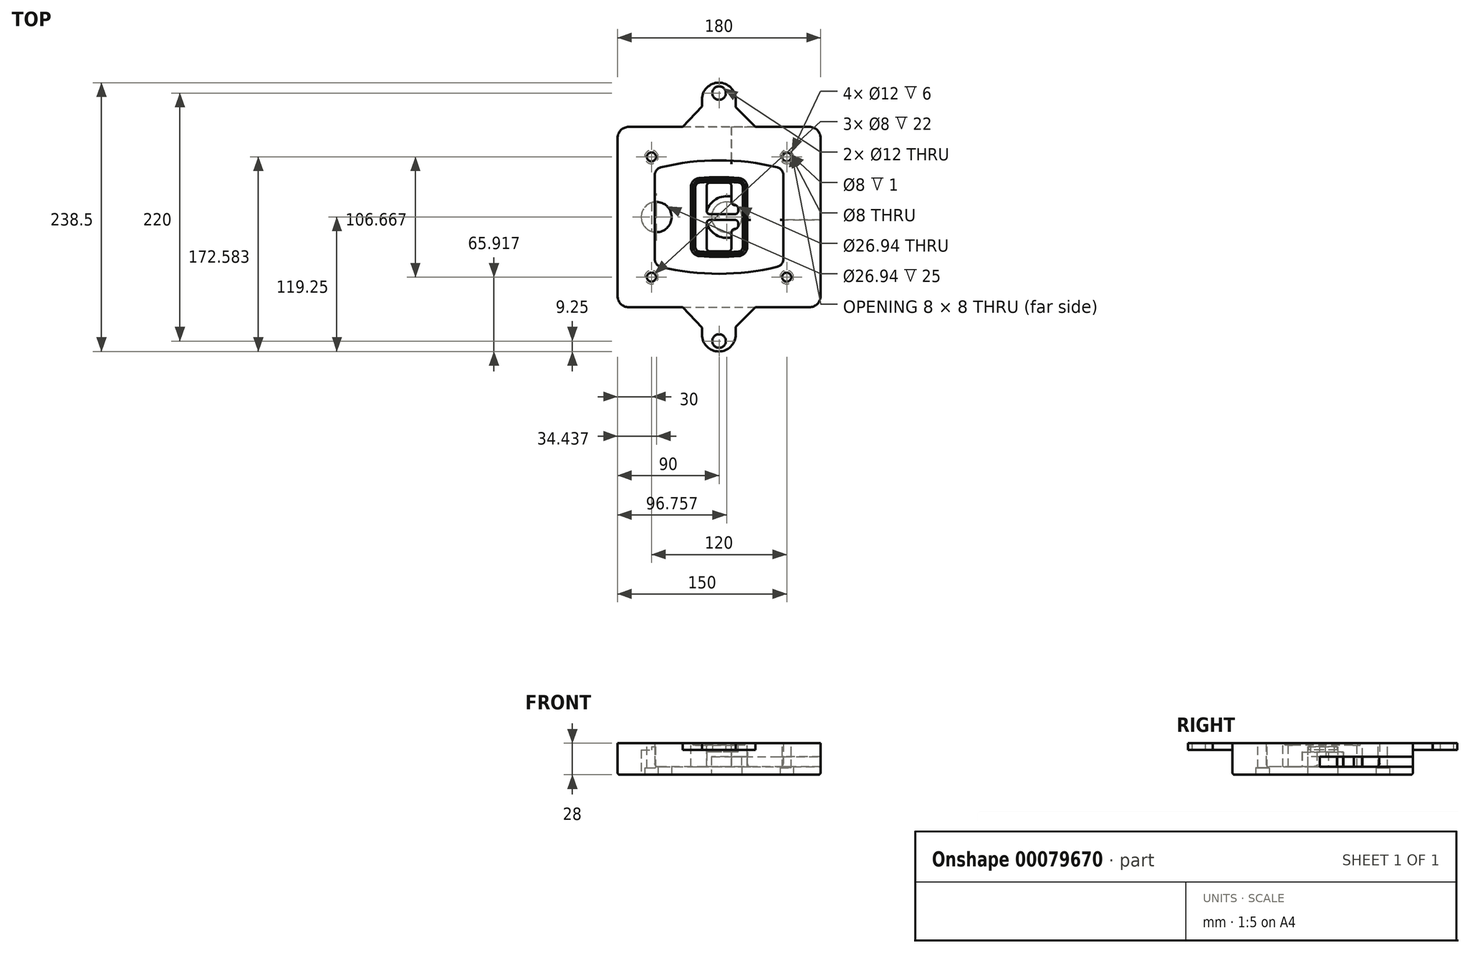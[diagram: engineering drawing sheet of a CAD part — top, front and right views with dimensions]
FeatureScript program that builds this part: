
annotation { "Feature Type Name" : "Feature", "Feature Type Description" : "" }
export const myFeature = defineFeature(function(context is Context, id is Id, definition is map)
    precondition{}
    {
        {
            var Q0;
            Q0=qCreatedBy(makeId("Top.planeOp"),FACE);
            var sketch = newSketch(context, id + "F0", { "sketchPlane" : qUnion([Q0])});
            skPoint(sketch, "E0.rect.middle", {"position": v(0, 0) * mm});
            skLineSegment(sketch, "E1.bottom", {"start": v(-80, -80) * mm, "end": v(80, -80) * mm});
            skLineSegment(sketch, "E1.top", {"start": v(-80, 80) * mm, "end": v(80, 80) * mm});
            skLineSegment(sketch, "E1.left", {"start": v(-90, -70) * mm, "end": v(-90, 70) * mm});
            skLineSegment(sketch, "E1.right", {"start": v(90, -70) * mm, "end": v(90, 70) * mm});
            skLineSegment(sketch, "E2", {"start": v(-90, 80) * mm, "end": v(90, -80) * mm, "construction": true});
            skLineSegment(sketch, "E3", {"start": v(90, 80) * mm, "end": v(-90, -80) * mm, "construction": true});
            skCircle(sketch, "E4", {"center": v(-60, 53.33) * mm, "radius": 4 * mm});
            skCircle(sketch, "E5", {"center": v(60, 53.33) * mm, "radius": 4 * mm});
            skCircle(sketch, "E6", {"center": v(60, -53.33) * mm, "radius": 4 * mm});
            skCircle(sketch, "E7", {"center": v(-60, -53.33) * mm, "radius": 4 * mm});
            skLineSegment(sketch, "E8", {"start": v(-60, 53.33) * mm, "end": v(60, 53.33) * mm, "construction": true});
            skLineSegment(sketch, "E9", {"start": v(60, 53.33) * mm, "end": v(60, -53.33) * mm, "construction": true});
            skLineSegment(sketch, "E10", {"start": v(60, -53.33) * mm, "end": v(-60, -53.33) * mm, "construction": true});
            skLineSegment(sketch, "E11", {"start": v(-60, -53.33) * mm, "end": v(-60, 53.33) * mm, "construction": true});
            skLineSegment(sketch, "E12", {"start": v(-60, 37.3) * mm, "end": v(-60, -37.3) * mm});
            skLineSegment(sketch, "E13", {"start": v(60, 37.3) * mm, "end": v(60, -37.3) * mm});
            skArc(sketch, "E14", {"start": v(52.38, 47.01) * mm, "mid": v(0, 53.33) * mm, "end": v(-52.38, 47.01) * mm});
            skArc(sketch, "E15", {"start": v(-52.38, -47.01) * mm, "mid": v(0, -53.33) * mm, "end": v(52.38, -47.01) * mm});
            skLineSegment(sketch, "E16", {"start": v(-60, 0) * mm, "end": v(60, 0) * mm, "construction": true});
            skPoint(sketch, "E17.visualSharp", {"position": v(-60, -45) * mm});
            skArc(sketch, "E17.filletArc", {"start": v(-60, -37.3) * mm, "mid": v(-57.87, -43.47) * mm, "end": v(-52.38, -47.01) * mm});
            skPoint(sketch, "E18.visualSharp", {"position": v(-60, 45) * mm});
            skArc(sketch, "E18.filletArc", {"start": v(-52.38, 47.01) * mm, "mid": v(-57.87, 43.47) * mm, "end": v(-60, 37.3) * mm});
            skPoint(sketch, "E19.visualSharp", {"position": v(60, 45) * mm});
            skArc(sketch, "E19.filletArc", {"start": v(60, 37.3) * mm, "mid": v(57.87, 43.47) * mm, "end": v(52.38, 47.01) * mm});
            skPoint(sketch, "E20.visualSharp", {"position": v(60, -45) * mm});
            skArc(sketch, "E20.filletArc", {"start": v(52.38, -47.01) * mm, "mid": v(57.87, -43.47) * mm, "end": v(60, -37.3) * mm});
            skPoint(sketch, "E21.visualSharp", {"position": v(-90, 80) * mm});
            skArc(sketch, "E21.filletArc", {"start": v(-80, 80) * mm, "mid": v(-87.07, 77.07) * mm, "end": v(-90, 70) * mm});
            skPoint(sketch, "E22.visualSharp", {"position": v(90, 80) * mm});
            skArc(sketch, "E22.filletArc", {"start": v(90, 70) * mm, "mid": v(87.07, 77.07) * mm, "end": v(80, 80) * mm});
            skPoint(sketch, "E23.visualSharp", {"position": v(90, -80) * mm});
            skArc(sketch, "E23.filletArc", {"start": v(80, -80) * mm, "mid": v(87.07, -77.07) * mm, "end": v(90, -70) * mm});
            skPoint(sketch, "E24.visualSharp", {"position": v(-90, -80) * mm});
            skArc(sketch, "E24.filletArc", {"start": v(-90, -70) * mm, "mid": v(-87.07, -77.07) * mm, "end": v(-80, -80) * mm});
            skArc(sketch, "E25.0", {"start": v(57, 37.3) * mm, "mid": v(55.5, 41.62) * mm, "end": v(51.67, 44.1) * mm});
            skLineSegment(sketch, "E25.1", {"start": v(57, 37.3) * mm, "end": v(57, -37.3) * mm});
            skArc(sketch, "E25.2", {"start": v(51.67, -44.1) * mm, "mid": v(55.5, -41.62) * mm, "end": v(57, -37.3) * mm});
            skArc(sketch, "E25.3", {"start": v(-51.67, -44.1) * mm, "mid": v(0, -50.33) * mm, "end": v(51.67, -44.1) * mm});
            skArc(sketch, "E25.4", {"start": v(-57, -37.3) * mm, "mid": v(-55.5, -41.62) * mm, "end": v(-51.67, -44.1) * mm});
            skArc(sketch, "E25.5", {"start": v(51.67, 44.1) * mm, "mid": v(0, 50.33) * mm, "end": v(-51.67, 44.1) * mm});
            skLineSegment(sketch, "E25.6", {"start": v(-57, 37.3) * mm, "end": v(-57, -37.3) * mm});
            skArc(sketch, "E25.7", {"start": v(-51.67, 44.1) * mm, "mid": v(-55.5, 41.62) * mm, "end": v(-57, 37.3) * mm});
            skArc(sketch, "E26.0", {"start": v(-53.33, 50.9) * mm, "mid": v(-61.01, 45.94) * mm, "end": v(-64, 37.3) * mm});
            skArc(sketch, "E26.1", {"start": v(53.33, 50.9) * mm, "mid": v(0, 57.33) * mm, "end": v(-53.33, 50.9) * mm});
            skArc(sketch, "E26.2", {"start": v(64, 37.3) * mm, "mid": v(61.01, 45.94) * mm, "end": v(53.33, 50.9) * mm});
            skLineSegment(sketch, "E26.3", {"start": v(64, 37.3) * mm, "end": v(64, -37.3) * mm});
            skArc(sketch, "E26.4", {"start": v(53.33, -50.9) * mm, "mid": v(61.01, -45.94) * mm, "end": v(64, -37.3) * mm});
            skLineSegment(sketch, "E26.5", {"start": v(-64, 37.3) * mm, "end": v(-64, -37.3) * mm});
            skArc(sketch, "E26.6", {"start": v(-53.33, -50.9) * mm, "mid": v(0, -57.33) * mm, "end": v(53.33, -50.9) * mm});
            skArc(sketch, "E26.7", {"start": v(-64, -37.3) * mm, "mid": v(-61.01, -45.94) * mm, "end": v(-53.33, -50.9) * mm});
            skSolve(sketch);
        }
        {
            var Q0;
            Q0=makeQuery(id+"F0.imprint","IMPRINT",FACE,{"disambiguationData":[TD([[makeQuery(id+"F0.imprint","IMPRINT",EDGE,{"derivedFrom":sQuery(id+"F0.wireOp",EDGE,"E1.bottom")}),1.0]])]});
            var Q1;
            Q1=makeQuery(id+"F0.imprint","IMPRINT",FACE,{"disambiguationData":[TD([[makeQuery(id+"F0.imprint","IMPRINT",EDGE,{"derivedFrom":sQuery(id+"F0.wireOp",EDGE,"E12")}),1.0]])]});
            var Q2;
            Q2=makeQuery(id+"F0.imprint","IMPRINT",FACE,{"disambiguationData":[TD([[makeQuery(id+"F0.imprint","IMPRINT",EDGE,{"derivedFrom":sQuery(id+"F0.wireOp",EDGE,"E25.0")}),1.0]])]});
            var Q3;
            Q3=makeQuery(id+"F0.imprint","IMPRINT",FACE,{"disambiguationData":[TD([[makeQuery(id+"F0.imprint","IMPRINT",EDGE,{"derivedFrom":sQuery(id+"F0.wireOp",EDGE,"E12")}),-1.0]])]});
            extrude(context, id + "F1", {"entities" : qUnion([Q0, Q1, Q2, Q3]), "oppositeDirection" : true, "depth" : 25 * mm});
        }
        {
            var Q0;
            Q0=makeQuery(id+"F0.imprint","IMPRINT",FACE,{"disambiguationData":[TD([[makeQuery(id+"F0.imprint","IMPRINT",EDGE,{"derivedFrom":sQuery(id+"F0.wireOp",EDGE,"E12")}),1.0]])]});
            extrude(context, id + "F2", {"entities" : qUnion([Q0]), "operationType" : NewBodyOperationType.ADD, "depth" : 3 * mm});
        }
        {
            var Q0;
            Q0=makeQuery(id+"F0.imprint","IMPRINT",FACE,{"disambiguationData":[TD([[makeQuery(id+"F0.imprint","IMPRINT",EDGE,{"derivedFrom":sQuery(id+"F0.wireOp",EDGE,"E25.0")}),1.0]])]});
            extrude(context, id + "F3", {"entities" : qUnion([Q0]), "operationType" : NewBodyOperationType.REMOVE, "oppositeDirection" : true, "depth" : 18 * mm});
        }
        {
            var Q0;
            Q0=makeQuery(id+"F2.opExtrude","CAP_FACE",FACE,{"disambiguationData":[OSD([sQuery(id+"F0.wireOp",EDGE,"E12"),sQuery(id+"F0.wireOp",EDGE,"E13"),sQuery(id+"F0.wireOp",EDGE,"E14"),sQuery(id+"F0.wireOp",EDGE,"E15"),sQuery(id+"F0.wireOp",EDGE,"E17.filletArc"),sQuery(id+"F0.wireOp",EDGE,"E18.filletArc"),sQuery(id+"F0.wireOp",EDGE,"E19.filletArc"),sQuery(id+"F0.wireOp",EDGE,"E20.filletArc"),sQuery(id+"F0.wireOp",EDGE,"E25.0"),sQuery(id+"F0.wireOp",EDGE,"E25.1"),sQuery(id+"F0.wireOp",EDGE,"E25.2"),sQuery(id+"F0.wireOp",EDGE,"E25.3"),sQuery(id+"F0.wireOp",EDGE,"E25.4"),sQuery(id+"F0.wireOp",EDGE,"E25.5"),sQuery(id+"F0.wireOp",EDGE,"E25.6"),sQuery(id+"F0.wireOp",EDGE,"E25.7")])],"isStart":false});
            var sketch = newSketch(context, id + "F4", { "sketchPlane" : qUnion([Q0])});
            skArc(sketch, "E27.0", {"start": v(-17.7, -34.56) * mm, "mid": v(0, -35.33) * mm, "end": v(17.7, -34.56) * mm});
            skArc(sketch, "E28.0", {"start": v(17.7, 34.56) * mm, "mid": v(0, 35.33) * mm, "end": v(-17.7, 34.56) * mm});
            skLineSegment(sketch, "E29", {"start": v(-25, 26.59) * mm, "end": v(-25, -26.59) * mm});
            skLineSegment(sketch, "E30", {"start": v(25, 26.59) * mm, "end": v(25, -26.59) * mm});
            skLineSegment(sketch, "E31", {"start": v(-25, 33.78) * mm, "end": v(25, 33.78) * mm, "construction": true});
            skLineSegment(sketch, "E32", {"start": v(-25, -33.78) * mm, "end": v(25, -33.78) * mm, "construction": true});
            skPoint(sketch, "E33.visualSharp", {"position": v(-25, 33.78) * mm});
            skArc(sketch, "E33.filletArc", {"start": v(-17.7, 34.56) * mm, "mid": v(-22.9, 32) * mm, "end": v(-25, 26.59) * mm});
            skPoint(sketch, "E34.visualSharp", {"position": v(25, 33.78) * mm});
            skArc(sketch, "E34.filletArc", {"start": v(25, 26.59) * mm, "mid": v(22.9, 32) * mm, "end": v(17.7, 34.56) * mm});
            skPoint(sketch, "E35.visualSharp", {"position": v(25, -33.78) * mm});
            skArc(sketch, "E35.filletArc", {"start": v(17.7, -34.56) * mm, "mid": v(22.9, -32) * mm, "end": v(25, -26.59) * mm});
            skPoint(sketch, "E36.visualSharp", {"position": v(-25, -33.78) * mm});
            skArc(sketch, "E36.filletArc", {"start": v(-25, -26.59) * mm, "mid": v(-22.9, -32) * mm, "end": v(-17.7, -34.56) * mm});
            skArc(sketch, "E37.0", {"start": v(51.67, 44.1) * mm, "mid": v(0, 50.33) * mm, "end": v(-51.67, 44.1) * mm});
            skArc(sketch, "E37.1", {"start": v(-51.67, 44.1) * mm, "mid": v(-55.5, 41.62) * mm, "end": v(-57, 37.3) * mm});
            skLineSegment(sketch, "E37.2", {"start": v(-57, 37.3) * mm, "end": v(-57, -37.3) * mm});
            skArc(sketch, "E37.3", {"start": v(-57, -37.3) * mm, "mid": v(-55.5, -41.62) * mm, "end": v(-51.67, -44.1) * mm});
            skArc(sketch, "E37.4", {"start": v(-51.67, -44.1) * mm, "mid": v(0, -50.33) * mm, "end": v(51.67, -44.1) * mm});
            skArc(sketch, "E37.5", {"start": v(51.67, -44.1) * mm, "mid": v(55.5, -41.62) * mm, "end": v(57, -37.3) * mm});
            skLineSegment(sketch, "E37.6", {"start": v(57, 37.3) * mm, "end": v(57, -37.3) * mm});
            skArc(sketch, "E37.7", {"start": v(57, 37.3) * mm, "mid": v(55.5, 41.62) * mm, "end": v(51.67, 44.1) * mm});
            skLineSegment(sketch, "E38.0", {"start": v(23, 26.59) * mm, "end": v(23, -26.59) * mm});
            skArc(sketch, "E38.1", {"start": v(17.53, -32.56) * mm, "mid": v(21.42, -30.64) * mm, "end": v(23, -26.59) * mm});
            skArc(sketch, "E38.2", {"start": v(-17.53, -32.56) * mm, "mid": v(0, -33.33) * mm, "end": v(17.53, -32.56) * mm});
            skArc(sketch, "E38.3", {"start": v(-23, -26.59) * mm, "mid": v(-21.42, -30.64) * mm, "end": v(-17.53, -32.56) * mm});
            skLineSegment(sketch, "E38.4", {"start": v(-23, 26.59) * mm, "end": v(-23, -26.59) * mm});
            skArc(sketch, "E38.5", {"start": v(23, 26.59) * mm, "mid": v(21.42, 30.64) * mm, "end": v(17.53, 32.56) * mm});
            skArc(sketch, "E38.6", {"start": v(-17.53, 32.56) * mm, "mid": v(-21.42, 30.64) * mm, "end": v(-23, 26.59) * mm});
            skArc(sketch, "E38.7", {"start": v(17.53, 32.56) * mm, "mid": v(0, 33.33) * mm, "end": v(-17.53, 32.56) * mm});
            skArc(sketch, "E39.0", {"start": v(21, 26.59) * mm, "mid": v(19.95, 29.29) * mm, "end": v(17.35, 30.57) * mm});
            skLineSegment(sketch, "E39.1", {"start": v(21, 26.59) * mm, "end": v(21, -26.59) * mm});
            skArc(sketch, "E39.2", {"start": v(17.35, -30.57) * mm, "mid": v(19.95, -29.29) * mm, "end": v(21, -26.59) * mm});
            skArc(sketch, "E39.3", {"start": v(-17.35, -30.57) * mm, "mid": v(0, -31.33) * mm, "end": v(17.35, -30.57) * mm});
            skArc(sketch, "E39.4", {"start": v(-21, -26.59) * mm, "mid": v(-19.95, -29.29) * mm, "end": v(-17.35, -30.57) * mm});
            skArc(sketch, "E39.5", {"start": v(17.35, 30.57) * mm, "mid": v(0, 31.33) * mm, "end": v(-17.35, 30.57) * mm});
            skLineSegment(sketch, "E39.6", {"start": v(-21, 26.59) * mm, "end": v(-21, -26.59) * mm});
            skArc(sketch, "E39.7", {"start": v(-17.35, 30.57) * mm, "mid": v(-19.95, 29.29) * mm, "end": v(-21, 26.59) * mm});
            skLineSegment(sketch, "E40", {"start": v(-25, 0) * mm, "end": v(25, 0) * mm, "construction": true});
            skLineSegment(sketch, "E41", {"start": v(-11, 5.5) * mm, "end": v(-11, 27.5) * mm});
            skLineSegment(sketch, "E42", {"start": v(-8, 30.5) * mm, "end": v(8, 30.5) * mm});
            skLineSegment(sketch, "E43", {"start": v(11, 27.5) * mm, "end": v(11, 13.5) * mm});
            skLineSegment(sketch, "E44", {"start": v(14, 10.5) * mm, "end": v(14, 10.5) * mm});
            skLineSegment(sketch, "E45", {"start": v(17, 7.5) * mm, "end": v(17, 5.5) * mm});
            skLineSegment(sketch, "E46", {"start": v(14, 2.5) * mm, "end": v(-8, 2.5) * mm});
            skPoint(sketch, "E47.visualSharp", {"position": v(-11, 30.5) * mm});
            skArc(sketch, "E47.filletArc", {"start": v(-8, 30.5) * mm, "mid": v(-10.12, 29.62) * mm, "end": v(-11, 27.5) * mm});
            skPoint(sketch, "E48.visualSharp", {"position": v(11, 30.5) * mm});
            skArc(sketch, "E48.filletArc", {"start": v(11, 27.5) * mm, "mid": v(10.12, 29.62) * mm, "end": v(8, 30.5) * mm});
            skPoint(sketch, "E49.visualSharp", {"position": v(11, 10.5) * mm});
            skArc(sketch, "E49.filletArc", {"start": v(11, 13.5) * mm, "mid": v(11.88, 11.38) * mm, "end": v(14, 10.5) * mm});
            skPoint(sketch, "E50.visualSharp", {"position": v(17, 10.5) * mm});
            skArc(sketch, "E50.filletArc", {"start": v(17, 7.5) * mm, "mid": v(16.12, 9.62) * mm, "end": v(14, 10.5) * mm});
            skPoint(sketch, "E51.visualSharp", {"position": v(17, 2.5) * mm});
            skArc(sketch, "E51.filletArc", {"start": v(14, 2.5) * mm, "mid": v(16.12, 3.38) * mm, "end": v(17, 5.5) * mm});
            skPoint(sketch, "E52.visualSharp", {"position": v(-11, 2.5) * mm});
            skArc(sketch, "E52.filletArc", {"start": v(-11, 5.5) * mm, "mid": v(-10.12, 3.38) * mm, "end": v(-8, 2.5) * mm});
            skLineSegment(sketch, "E53.0.MirrorCS", {"start": v(14, -2.5) * mm, "end": v(-8, -2.5) * mm});
            skArc(sketch, "E54.0.MirrorCS", {"start": v(-11, -5.5) * mm, "mid": v(-10.12, -3.38) * mm, "end": v(-8, -2.5) * mm});
            skLineSegment(sketch, "E55.0.MirrorCS", {"start": v(-11, -5.5) * mm, "end": v(-11, -27.5) * mm});
            skArc(sketch, "E56.0.MirrorCS", {"start": v(-8, -30.5) * mm, "mid": v(-10.12, -29.62) * mm, "end": v(-11, -27.5) * mm});
            skLineSegment(sketch, "E57.0.MirrorCS", {"start": v(-8, -30.5) * mm, "end": v(8, -30.5) * mm});
            skArc(sketch, "E58.0.MirrorCS", {"start": v(11, -27.5) * mm, "mid": v(10.12, -29.62) * mm, "end": v(8, -30.5) * mm});
            skLineSegment(sketch, "E59.0.MirrorCS", {"start": v(11, -27.5) * mm, "end": v(11, -13.5) * mm});
            skArc(sketch, "E60.0.MirrorCS", {"start": v(11, -13.5) * mm, "mid": v(11.88, -11.38) * mm, "end": v(14, -10.5) * mm});
            skArc(sketch, "E61.0.MirrorCS", {"start": v(17, -7.5) * mm, "mid": v(16.12, -9.62) * mm, "end": v(14, -10.5) * mm});
            skLineSegment(sketch, "E62.0.MirrorCS", {"start": v(17, -7.5) * mm, "end": v(17, -5.5) * mm});
            skArc(sketch, "E63.0.MirrorCS", {"start": v(14, -2.5) * mm, "mid": v(16.12, -3.38) * mm, "end": v(17, -5.5) * mm});
            skSolve(sketch);
        }
        {
            var Q0;
            Q0=makeQuery(id+"F4.imprint","IMPRINT",FACE,{"disambiguationData":[TD([[makeQuery(id+"F4.imprint","IMPRINT",EDGE,{"derivedFrom":sQuery(id+"F4.wireOp",EDGE,"E27.0")}),1.0]])]});
            var Q1;
            Q1=makeQuery(id+"F4.imprint","IMPRINT",FACE,{"disambiguationData":[TD([[makeQuery(id+"F4.imprint","IMPRINT",EDGE,{"derivedFrom":sQuery(id+"F4.wireOp",EDGE,"E38.0")}),-1.0]])]});
            var Q2;
            Q2=makeQuery(id+"F4.imprint","IMPRINT",FACE,{"disambiguationData":[TD([[makeQuery(id+"F4.imprint","IMPRINT",EDGE,{"derivedFrom":sQuery(id+"F4.wireOp",EDGE,"E39.0")}),1.0]])]});
            extrude(context, id + "F5", {"entities" : qUnion([Q0, Q1, Q2]), "operationType" : NewBodyOperationType.ADD, "endBound" : BoundingType.UP_TO_NEXT, "oppositeDirection" : true, "depth" : 25 * mm});
        }
        {
            var Q0;
            Q0=makeQuery(id+"F4.imprint","IMPRINT",FACE,{"disambiguationData":[TD([[makeQuery(id+"F4.imprint","IMPRINT",EDGE,{"derivedFrom":sQuery(id+"F4.wireOp",EDGE,"E38.0")}),-1.0]])]});
            extrude(context, id + "F6", {"entities" : qUnion([Q0]), "operationType" : NewBodyOperationType.REMOVE, "oppositeDirection" : true, "depth" : 2 * mm});
        }
        {
            var Q0;
            Q0=makeQuery(id+"F1.opExtrude","CAP_FACE",FACE,{"disambiguationData":[OSD([sQuery(id+"F0.wireOp",EDGE,"E1.bottom"),sQuery(id+"F0.wireOp",EDGE,"E1.top"),sQuery(id+"F0.wireOp",EDGE,"E1.left"),sQuery(id+"F0.wireOp",EDGE,"E1.right"),sQuery(id+"F0.wireOp",EDGE,"E4"),sQuery(id+"F0.wireOp",EDGE,"E5"),sQuery(id+"F0.wireOp",EDGE,"E6"),sQuery(id+"F0.wireOp",EDGE,"E7"),sQuery(id+"F0.wireOp",EDGE,"E21.filletArc"),sQuery(id+"F0.wireOp",EDGE,"E22.filletArc"),sQuery(id+"F0.wireOp",EDGE,"E23.filletArc"),sQuery(id+"F0.wireOp",EDGE,"E24.filletArc")])],"isStart":false});
            var sketch = newSketch(context, id + "F7", { "sketchPlane" : qUnion([Q0])});
            skCircle(sketch, "E64", {"center": v(6.76, 0) * mm, "radius": 13.47 * mm});
            skCircle(sketch, "E65", {"center": v(-55.56, 0) * mm, "radius": 13.47 * mm});
            skLineSegment(sketch, "E66", {"start": v(90, 0) * mm, "end": v(-90, 0) * mm});
            skCircle(sketch, "E67", {"center": v(6.76, 0) * mm, "radius": 18.47 * mm});
            skCircle(sketch, "E68", {"center": v(60, -53.33) * mm, "radius": 6 * mm});
            skCircle(sketch, "E69", {"center": v(-60, -53.33) * mm, "radius": 6 * mm});
            skCircle(sketch, "E70", {"center": v(-60, 53.33) * mm, "radius": 6 * mm});
            skCircle(sketch, "E71", {"center": v(60, 53.33) * mm, "radius": 6 * mm});
            skSolve(sketch);
        }
        {
            var Q0;
            {var subQ1=sQuery(id+"F7.wireOp",EDGE,"E66");var subQ4=sQuery(id+"F7.wireOp",EDGE,"E64");var subQ6=makeQuery(id+"F7.imprint","INTERSECT",VERTEX,{"disambiguationData":[OD(0.0)],"derivedFrom":[subQ4,subQ1]});Q0=makeQuery(id+"F7.imprint","IMPRINT",FACE,{"disambiguationData":[TD([[makeQuery(id+"F7.imprint","IMPRINT",EDGE,{"disambiguationData":[TD([[subQ6,-1.0]])],"derivedFrom":subQ4}),-1.0]])]});}
            var Q1;
            {var subQ0=sQuery(id+"F7.wireOp",EDGE,"E66");var subQ1=sQuery(id+"F7.wireOp",EDGE,"E64");var subQ3=makeQuery(id+"F7.imprint","INTERSECT",VERTEX,{"disambiguationData":[OD(0.0)],"derivedFrom":[subQ1,subQ0]});Q1=makeQuery(id+"F7.imprint","IMPRINT",FACE,{"disambiguationData":[TD([[makeQuery(id+"F7.imprint","IMPRINT",EDGE,{"disambiguationData":[TD([[subQ3,-1.0]])],"derivedFrom":subQ1}),1.0]])]});}
            var Q2;
            {var subQ0=sQuery(id+"F7.wireOp",EDGE,"E66");var subQ1=sQuery(id+"F7.wireOp",EDGE,"E64");var subQ3=makeQuery(id+"F7.imprint","INTERSECT",VERTEX,{"disambiguationData":[OD(0.0)],"derivedFrom":[subQ1,subQ0]});Q2=makeQuery(id+"F7.imprint","IMPRINT",FACE,{"disambiguationData":[TD([[makeQuery(id+"F7.imprint","IMPRINT",EDGE,{"disambiguationData":[TD([[subQ3,1.0]])],"derivedFrom":subQ1}),1.0]])]});}
            var Q3;
            {var subQ1=sQuery(id+"F7.wireOp",EDGE,"E66");var subQ4=sQuery(id+"F7.wireOp",EDGE,"E64");var subQ6=makeQuery(id+"F7.imprint","INTERSECT",VERTEX,{"disambiguationData":[OD(0.0)],"derivedFrom":[subQ4,subQ1]});Q3=makeQuery(id+"F7.imprint","IMPRINT",FACE,{"disambiguationData":[TD([[makeQuery(id+"F7.imprint","IMPRINT",EDGE,{"disambiguationData":[TD([[subQ6,1.0]])],"derivedFrom":subQ4}),-1.0]])]});}
            extrude(context, id + "F8", {"entities" : qUnion([Q0, Q1, Q2, Q3]), "operationType" : NewBodyOperationType.ADD, "oppositeDirection" : true, "depth" : 20 * mm});
        }
        {
            var Q0;
            {var subQ0=sQuery(id+"F7.wireOp",EDGE,"E66");var subQ1=sQuery(id+"F7.wireOp",EDGE,"E64");var subQ3=makeQuery(id+"F7.imprint","INTERSECT",VERTEX,{"disambiguationData":[OD(0.0)],"derivedFrom":[subQ1,subQ0]});Q0=makeQuery(id+"F7.imprint","IMPRINT",FACE,{"disambiguationData":[TD([[makeQuery(id+"F7.imprint","IMPRINT",EDGE,{"disambiguationData":[TD([[subQ3,-1.0]])],"derivedFrom":subQ1}),1.0]])]});}
            var Q1;
            {var subQ0=sQuery(id+"F7.wireOp",EDGE,"E66");var subQ1=sQuery(id+"F7.wireOp",EDGE,"E64");var subQ3=makeQuery(id+"F7.imprint","INTERSECT",VERTEX,{"disambiguationData":[OD(0.0)],"derivedFrom":[subQ1,subQ0]});Q1=makeQuery(id+"F7.imprint","IMPRINT",FACE,{"disambiguationData":[TD([[makeQuery(id+"F7.imprint","IMPRINT",EDGE,{"disambiguationData":[TD([[subQ3,1.0]])],"derivedFrom":subQ1}),1.0]])]});}
            extrude(context, id + "F9", {"entities" : qUnion([Q0, Q1]), "operationType" : NewBodyOperationType.REMOVE, "oppositeDirection" : true, "depth" : 16 * mm});
        }
        {
            var Q0;
            {var subQ0=sQuery(id+"F7.wireOp",EDGE,"E66");var subQ1=sQuery(id+"F7.wireOp",EDGE,"E65");var subQ3=makeQuery(id+"F7.imprint","INTERSECT",VERTEX,{"disambiguationData":[OD(0.0)],"derivedFrom":[subQ1,subQ0]});Q0=makeQuery(id+"F7.imprint","IMPRINT",FACE,{"disambiguationData":[TD([[makeQuery(id+"F7.imprint","IMPRINT",EDGE,{"disambiguationData":[TD([[subQ3,-1.0]])],"derivedFrom":subQ1}),1.0]])]});}
            var Q1;
            {var subQ0=sQuery(id+"F7.wireOp",EDGE,"E66");var subQ1=sQuery(id+"F7.wireOp",EDGE,"E65");var subQ3=makeQuery(id+"F7.imprint","INTERSECT",VERTEX,{"disambiguationData":[OD(0.0)],"derivedFrom":[subQ1,subQ0]});Q1=makeQuery(id+"F7.imprint","IMPRINT",FACE,{"disambiguationData":[TD([[makeQuery(id+"F7.imprint","IMPRINT",EDGE,{"disambiguationData":[TD([[subQ3,1.0]])],"derivedFrom":subQ1}),1.0]])]});}
            extrude(context, id + "F10", {"entities" : qUnion([Q0, Q1]), "operationType" : NewBodyOperationType.REMOVE, "oppositeDirection" : true, "depth" : 25 * mm});
        }
        {
            var Q0;
            Q0=makeQuery(id+"F7.imprint","IMPRINT",FACE,{"disambiguationData":[TD([[makeQuery(id+"F7.imprint","IMPRINT",EDGE,{"derivedFrom":sQuery(id+"F7.wireOp",EDGE,"E68")}),1.0]])]});
            var Q1;
            Q1=makeQuery(id+"F7.imprint","IMPRINT",FACE,{"disambiguationData":[TD([[makeQuery(id+"F7.imprint","IMPRINT",EDGE,{"derivedFrom":makeQuery(id+"F1.opExtrude","CAP_EDGE",EDGE,{"disambiguationData":[OSD([sQuery(id+"F0.wireOp",EDGE,"E5")])],"isStart":false})}),-1.0]])]});
            var Q2;
            Q2=makeQuery(id+"F7.imprint","IMPRINT",FACE,{"disambiguationData":[TD([[makeQuery(id+"F7.imprint","IMPRINT",EDGE,{"derivedFrom":sQuery(id+"F7.wireOp",EDGE,"E69")}),1.0]])]});
            var Q3;
            Q3=makeQuery(id+"F7.imprint","IMPRINT",FACE,{"disambiguationData":[TD([[makeQuery(id+"F7.imprint","IMPRINT",EDGE,{"derivedFrom":makeQuery(id+"F1.opExtrude","CAP_EDGE",EDGE,{"disambiguationData":[OSD([sQuery(id+"F0.wireOp",EDGE,"E4")])],"isStart":false})}),-1.0]])]});
            var Q4;
            Q4=makeQuery(id+"F7.imprint","IMPRINT",FACE,{"disambiguationData":[TD([[makeQuery(id+"F7.imprint","IMPRINT",EDGE,{"derivedFrom":sQuery(id+"F7.wireOp",EDGE,"E70")}),1.0]])]});
            var Q5;
            Q5=makeQuery(id+"F7.imprint","IMPRINT",FACE,{"disambiguationData":[TD([[makeQuery(id+"F7.imprint","IMPRINT",EDGE,{"derivedFrom":makeQuery(id+"F1.opExtrude","CAP_EDGE",EDGE,{"disambiguationData":[OSD([sQuery(id+"F0.wireOp",EDGE,"E7")])],"isStart":false})}),-1.0]])]});
            var Q6;
            Q6=makeQuery(id+"F7.imprint","IMPRINT",FACE,{"disambiguationData":[TD([[makeQuery(id+"F7.imprint","IMPRINT",EDGE,{"derivedFrom":sQuery(id+"F7.wireOp",EDGE,"E71")}),1.0]])]});
            var Q7;
            Q7=makeQuery(id+"F7.imprint","IMPRINT",FACE,{"disambiguationData":[TD([[makeQuery(id+"F7.imprint","IMPRINT",EDGE,{"derivedFrom":makeQuery(id+"F1.opExtrude","CAP_EDGE",EDGE,{"disambiguationData":[OSD([sQuery(id+"F0.wireOp",EDGE,"E6")])],"isStart":false})}),-1.0]])]});
            extrude(context, id + "F11", {"entities" : qUnion([Q0, Q1, Q2, Q3, Q4, Q5, Q6, Q7]), "operationType" : NewBodyOperationType.REMOVE, "oppositeDirection" : true, "depth" : 6 * mm});
        }
        {
            var Q0;
            Q0=makeQuery(id+"F9.boolean.opBoolean","COPY",FACE,{"derivedFrom":makeQuery(id+"F9.opExtrude","CAP_FACE",FACE,{"disambiguationData":[OSD([sQuery(id+"F7.wireOp",EDGE,"E64")])],"isStart":false})});
            var sketch = newSketch(context, id + "F12", { "sketchPlane" : qUnion([Q0])});
            skArc(sketch, "E72.0", {"start": v(11, -88.19) * mm, "mid": v(97.1, -83.6) * mm, "end": v(92.5, 2.5) * mm});
            skLineSegment(sketch, "E72.1", {"start": v(11, -17.97) * mm, "end": v(11, -17.97) * mm});
            skLineSegment(sketch, "E73", {"start": v(92.5, -105.13) * mm, "end": v(102.3, -105.13) * mm});
            skLineSegment(sketch, "E74.0", {"start": v(92.5, 2.5) * mm, "end": v(14, 2.5) * mm});
            skArc(sketch, "E74.1", {"start": v(14, 2.5) * mm, "mid": v(16.12, 3.38) * mm, "end": v(17, 5.5) * mm});
            skLineSegment(sketch, "E74.2", {"start": v(17, 7.5) * mm, "end": v(17, 5.5) * mm});
            skArc(sketch, "E74.3", {"start": v(17, 7.5) * mm, "mid": v(16.12, 9.62) * mm, "end": v(14, 10.5) * mm});
            skArc(sketch, "E74.4", {"start": v(11, 13.5) * mm, "mid": v(11.88, 11.38) * mm, "end": v(14, 10.5) * mm});
            skLineSegment(sketch, "E74.5", {"start": v(11, 13.5) * mm, "end": v(11, -88.19) * mm});
            skLineSegment(sketch, "E74.7", {"start": v(92.5, -2.5) * mm, "end": v(14, -2.5) * mm});
            skArc(sketch, "E74.8", {"start": v(14, -2.5) * mm, "mid": v(16.12, -3.38) * mm, "end": v(17, -5.5) * mm});
            skLineSegment(sketch, "E74.9", {"start": v(17, -7.5) * mm, "end": v(17, -5.5) * mm});
            skArc(sketch, "E74.10", {"start": v(17, -7.5) * mm, "mid": v(16.12, -9.62) * mm, "end": v(14, -10.5) * mm});
            skArc(sketch, "E74.11", {"start": v(11, -13.5) * mm, "mid": v(11.88, -11.38) * mm, "end": v(14, -10.5) * mm});
            skLineSegment(sketch, "E74.12", {"start": v(11, -17.97) * mm, "end": v(11, -13.5) * mm});
            skPoint(sketch, "E75.orphan", {"position": v(11, -27.5) * mm});
            skPoint(sketch, "E76.orphan", {"position": v(-8, -2.5) * mm});
            skPoint(sketch, "E77.orphan", {"position": v(-8, 2.5) * mm});
            skPoint(sketch, "E78.orphan", {"position": v(11, 27.5) * mm});
            skSolve(sketch);
        }
        {
            var Q0;
            {var subQ7=sQuery(id+"F12.wireOp",EDGE,"E72.0");var subQ14=sQuery(id+"F12.wireOp",EDGE,"E72.1");var subQ16=sQuery(id+"F12.wireOp",EDGE,"E74.1");var subQ18=sQuery(id+"F12.wireOp",EDGE,"E74.8");Q0=qUnion([makeQuery(id+"F12.imprint","IMPRINT",FACE,{"disambiguationData":[TD([[makeQuery(id+"F12.imprint","IMPRINT",EDGE,{"derivedFrom":subQ7}),1.0]])]}),makeQuery(id+"F12.imprint","IMPRINT",FACE,{"disambiguationData":[TD([[makeQuery(id+"F12.imprint","IMPRINT",EDGE,{"derivedFrom":subQ14}),1.0]])]}),makeQuery(id+"F12.imprint","IMPRINT",FACE,{"disambiguationData":[TD([[makeQuery(id+"F12.imprint","IMPRINT",EDGE,{"derivedFrom":subQ16}),1.0]])]}),makeQuery(id+"F12.imprint","IMPRINT",FACE,{"disambiguationData":[TD([[makeQuery(id+"F12.imprint","IMPRINT",EDGE,{"derivedFrom":subQ18}),-1.0]])]})]);}
            var Q1;
            Q1=makeQuery(id+"F5.boolean.opBoolean","SPLIT",FACE,{"disambiguationData":[TD([makeQuery(id+"F5.opExtrude","SWEPT_FACE",FACE,{"disambiguationData":[OSD([sQuery(id+"F4.wireOp",EDGE,"E41")])]})])],"derivedFrom":makeQuery(id+"F3.boolean.opBoolean","COPY",FACE,{"derivedFrom":makeQuery(id+"F3.opExtrude","CAP_FACE",FACE,{"disambiguationData":[OSD([sQuery(id+"F0.wireOp",EDGE,"E25.0"),sQuery(id+"F0.wireOp",EDGE,"E25.1"),sQuery(id+"F0.wireOp",EDGE,"E25.2"),sQuery(id+"F0.wireOp",EDGE,"E25.3"),sQuery(id+"F0.wireOp",EDGE,"E25.4"),sQuery(id+"F0.wireOp",EDGE,"E25.5"),sQuery(id+"F0.wireOp",EDGE,"E25.6"),sQuery(id+"F0.wireOp",EDGE,"E25.7")])],"isStart":false})})});
            extrude(context, id + "F13", {"entities" : qUnion([Q0]), "operationType" : NewBodyOperationType.REMOVE, "endBound" : BoundingType.UP_TO_SURFACE, "endBoundEntityFace" : qUnion([Q1]), "depth" : 25 * mm});
        }
        {
            var Q0;
            Q0=makeQuery(id+"F3.boolean.opBoolean","COPY",EDGE,{"derivedFrom":makeQuery(id+"F3.opExtrude","CAP_EDGE",EDGE,{"disambiguationData":[OSD([sQuery(id+"F0.wireOp",EDGE,"E25.6")])],"isStart":false})});
            var Q1;
            Q1=makeQuery(id+"F8.boolean.opBoolean","INTERSECT",EDGE,{"derivedFrom":[makeQuery(id+"F5.opExtrude","SWEPT_FACE",FACE,{"disambiguationData":[OSD([sQuery(id+"F4.wireOp",EDGE,"E30")])]}),makeQuery(id+"F8.opExtrude","CAP_FACE",FACE,{"disambiguationData":[OSD([sQuery(id+"F7.wireOp",EDGE,"E67")])],"isStart":false})]});
            var Q2;
            Q2=makeQuery(id+"F8.boolean.opBoolean","INTERSECT",EDGE,{"disambiguationData":[OD(1.0)],"derivedFrom":[makeQuery(id+"F5.opExtrude","SWEPT_FACE",FACE,{"disambiguationData":[OSD([sQuery(id+"F4.wireOp",EDGE,"E30")])]}),makeQuery(id+"F8.opExtrude","SWEPT_FACE",FACE,{"disambiguationData":[OSD([sQuery(id+"F7.wireOp",EDGE,"E67")])]})]});
            var Q3;
            {var subQ0=makeQuery(id+"F3.boolean.opBoolean","COPY",FACE,{"derivedFrom":makeQuery(id+"F3.opExtrude","CAP_FACE",FACE,{"disambiguationData":[OSD([sQuery(id+"F0.wireOp",EDGE,"E25.0"),sQuery(id+"F0.wireOp",EDGE,"E25.1"),sQuery(id+"F0.wireOp",EDGE,"E25.2"),sQuery(id+"F0.wireOp",EDGE,"E25.3"),sQuery(id+"F0.wireOp",EDGE,"E25.4"),sQuery(id+"F0.wireOp",EDGE,"E25.5"),sQuery(id+"F0.wireOp",EDGE,"E25.6"),sQuery(id+"F0.wireOp",EDGE,"E25.7")])],"isStart":false})});var subQ1=sQuery(id+"F4.wireOp",EDGE,"E30");Q3=makeQuery(id+"F8.boolean.opBoolean","SPLIT",EDGE,{"disambiguationData":[TD([makeQuery(id+"F5.opExtrude","SWEPT_FACE",FACE,{"disambiguationData":[OSD([sQuery(id+"F4.wireOp",EDGE,"E35.filletArc")])]})])],"derivedFrom":makeQuery(id+"F5.opExtrude","TWEAK_EDGE",EDGE,{"derivedFrom":[subQ0,makeQuery(id+"F4.imprint","IMPRINT",EDGE,{"derivedFrom":subQ1})]})});}
            var Q4;
            {var subQ0=sQuery(id+"F0.wireOp",EDGE,"E25.0");var subQ1=sQuery(id+"F0.wireOp",EDGE,"E25.1");var subQ2=sQuery(id+"F0.wireOp",EDGE,"E25.2");var subQ3=sQuery(id+"F0.wireOp",EDGE,"E25.3");var subQ4=sQuery(id+"F0.wireOp",EDGE,"E25.4");var subQ5=sQuery(id+"F0.wireOp",EDGE,"E25.5");var subQ6=sQuery(id+"F0.wireOp",EDGE,"E25.6");var subQ7=sQuery(id+"F0.wireOp",EDGE,"E25.7");Q4=makeQuery(id+"F8.boolean.opBoolean","INTERSECT",EDGE,{"derivedFrom":[makeQuery(id+"F5.boolean.opBoolean","SPLIT",FACE,{"disambiguationData":[TD([makeQuery(id+"F2.opExtrude","SWEPT_FACE",FACE,{"disambiguationData":[OSD([subQ0])]})])],"derivedFrom":makeQuery(id+"F3.boolean.opBoolean","COPY",FACE,{"derivedFrom":makeQuery(id+"F3.opExtrude","CAP_FACE",FACE,{"disambiguationData":[OSD([subQ0,subQ1,subQ2,subQ3,subQ4,subQ5,subQ6,subQ7])],"isStart":false})})}),makeQuery(id+"F8.opExtrude","SWEPT_FACE",FACE,{"disambiguationData":[OSD([sQuery(id+"F7.wireOp",EDGE,"E67")])]})]});}
            var Q5;
            Q5=makeQuery(id+"F8.boolean.opBoolean","INTERSECT",EDGE,{"disambiguationData":[OD(0.0)],"derivedFrom":[makeQuery(id+"F5.opExtrude","SWEPT_FACE",FACE,{"disambiguationData":[OSD([sQuery(id+"F4.wireOp",EDGE,"E30")])]}),makeQuery(id+"F8.opExtrude","SWEPT_FACE",FACE,{"disambiguationData":[OSD([sQuery(id+"F7.wireOp",EDGE,"E67")])]})]});
            fillet(context, id + "F14", {"entities" : qUnion([Q0, Q1, Q2, Q3, Q4, Q5]), "radius" : 3 * mm, "tangentPropagation" : true, "allowEdgeOverflow" : false});
        }
        {
            var Q0;
            Q0=makeQuery(id+"F1.opExtrude","CAP_EDGE",EDGE,{"disambiguationData":[OSD([sQuery(id+"F0.wireOp",EDGE,"E1.bottom")])],"isStart":false});
            fillet(context, id + "F15", {"entities" : qUnion([Q0]), "radius" : 2 * mm, "tangentPropagation" : true, "allowEdgeOverflow" : false});
        }
        {
            var Q0;
            {var subQ0=sQuery(id+"F0.wireOp",EDGE,"E22.filletArc");var subQ1=sQuery(id+"F0.wireOp",EDGE,"E7");var subQ2=sQuery(id+"F0.wireOp",EDGE,"E6");var subQ3=sQuery(id+"F0.wireOp",EDGE,"E5");var subQ4=sQuery(id+"F0.wireOp",EDGE,"E4");var subQ5=sQuery(id+"F0.wireOp",EDGE,"E1.bottom");var subQ6=sQuery(id+"F0.wireOp",EDGE,"E21.filletArc");var subQ7=sQuery(id+"F0.wireOp",EDGE,"E1.top");var subQ8=sQuery(id+"F0.wireOp",EDGE,"E1.left");var subQ9=sQuery(id+"F0.wireOp",EDGE,"E1.right");var subQ10=sQuery(id+"F0.wireOp",EDGE,"E23.filletArc");var subQ11=sQuery(id+"F0.wireOp",EDGE,"E24.filletArc");Q0=makeQuery(id+"F2.boolean.opBoolean","SPLIT",FACE,{"disambiguationData":[TD([makeQuery(id+"F1.opExtrude","SWEPT_FACE",FACE,{"disambiguationData":[OSD([subQ5])]})])],"derivedFrom":makeQuery(id+"F1.opExtrude","CAP_FACE",FACE,{"disambiguationData":[OSD([subQ5,subQ7,subQ8,subQ9,subQ4,subQ3,subQ2,subQ1,subQ6,subQ0,subQ10,subQ11])],"isStart":true})});}
            var sketch = newSketch(context, id + "F16", { "sketchPlane" : qUnion([Q0])});
            skArc(sketch, "E79.0", {"start": v(-80, 80) * mm, "mid": v(-87.07, 77.07) * mm, "end": v(-90, 70) * mm});
            skLineSegment(sketch, "E79.1", {"start": v(-90, -70) * mm, "end": v(-90, 70) * mm});
            skLineSegment(sketch, "E79.2", {"start": v(-80, 80) * mm, "end": v(80, 80) * mm});
            skArc(sketch, "E79.3", {"start": v(90, 70) * mm, "mid": v(87.07, 77.07) * mm, "end": v(80, 80) * mm});
            skLineSegment(sketch, "E79.4", {"start": v(90, -70) * mm, "end": v(90, 70) * mm});
            skArc(sketch, "E79.5", {"start": v(80, -80) * mm, "mid": v(87.07, -77.07) * mm, "end": v(90, -70) * mm});
            skLineSegment(sketch, "E79.6", {"start": v(-80, -80) * mm, "end": v(80, -80) * mm});
            skArc(sketch, "E79.7", {"start": v(-90, -70) * mm, "mid": v(-87.07, -77.07) * mm, "end": v(-80, -80) * mm});
            skCircle(sketch, "E79.8", {"center": v(-60, 53.33) * mm, "radius": 4 * mm});
            skCircle(sketch, "E79.9", {"center": v(60, 53.33) * mm, "radius": 4 * mm});
            skCircle(sketch, "E79.10", {"center": v(-60, -53.33) * mm, "radius": 4 * mm});
            skCircle(sketch, "E79.11", {"center": v(60, -53.33) * mm, "radius": 4 * mm});
            skArc(sketch, "E79.12", {"start": v(52.38, -47.01) * mm, "mid": v(57.87, -43.47) * mm, "end": v(60, -37.3) * mm});
            skLineSegment(sketch, "E79.13", {"start": v(60, 37.3) * mm, "end": v(60, -37.3) * mm});
            skArc(sketch, "E79.14", {"start": v(60, 37.3) * mm, "mid": v(57.87, 43.47) * mm, "end": v(52.38, 47.01) * mm});
            skArc(sketch, "E79.15", {"start": v(52.38, 47.01) * mm, "mid": v(0, 53.33) * mm, "end": v(-52.38, 47.01) * mm});
            skArc(sketch, "E79.16", {"start": v(-52.38, 47.01) * mm, "mid": v(-57.87, 43.47) * mm, "end": v(-60, 37.3) * mm});
            skLineSegment(sketch, "E79.17", {"start": v(-60, 37.3) * mm, "end": v(-60, -37.3) * mm});
            skArc(sketch, "E79.18", {"start": v(-60, -37.3) * mm, "mid": v(-57.87, -43.47) * mm, "end": v(-52.38, -47.01) * mm});
            skArc(sketch, "E79.19", {"start": v(-52.38, -47.01) * mm, "mid": v(0, -53.33) * mm, "end": v(52.38, -47.01) * mm});
            skLineSegment(sketch, "E80", {"start": v(0, 80) * mm, "end": v(0, 110) * mm, "construction": true});
            skCircle(sketch, "E81", {"center": v(0, 110) * mm, "radius": 6 * mm});
            skLineSegment(sketch, "E82", {"start": v(-32.29, 80) * mm, "end": v(-15.18, 98) * mm});
            skLineSegment(sketch, "E83", {"start": v(-15.18, 98) * mm, "end": v(-15.18, 104.25) * mm});
            skLineSegment(sketch, "E84", {"start": v(32.3, 80) * mm, "end": v(14.82, 97.47) * mm});
            skLineSegment(sketch, "E85", {"start": v(14.82, 97.47) * mm, "end": v(14.82, 104.25) * mm});
            skArc(sketch, "E86", {"start": v(14.82, 104.25) * mm, "mid": v(-0.18, 119.25) * mm, "end": v(-15.18, 104.25) * mm});
            skLineSegment(sketch, "E87", {"start": v(-131.24, 0) * mm, "end": v(132.18, 0) * mm, "construction": true});
            skPoint(sketch, "E87.startSnap0", {"position": v(-90, 0) * mm});
            skPoint(sketch, "E87.endSnap0", {"position": v(90, 0) * mm});
            skLineSegment(sketch, "E88.MirrorCS", {"start": v(14.82, -97.47) * mm, "end": v(14.82, -104.25) * mm});
            skLineSegment(sketch, "E89.MirrorCS", {"start": v(32.3, -80) * mm, "end": v(14.82, -97.47) * mm});
            skArc(sketch, "E90.MirrorCS", {"start": v(14.82, -104.25) * mm, "mid": v(-0.18, -119.25) * mm, "end": v(-15.18, -104.25) * mm});
            skLineSegment(sketch, "E91.MirrorCS", {"start": v(-15.18, -98) * mm, "end": v(-15.18, -104.25) * mm});
            skLineSegment(sketch, "E92.MirrorCS", {"start": v(-32.29, -80) * mm, "end": v(-15.18, -98) * mm});
            skLineSegment(sketch, "E93.MirrorCS", {"start": v(0, -80) * mm, "end": v(0, -110) * mm, "construction": true});
            skCircle(sketch, "E94.MirrorC", {"center": v(0, -110) * mm, "radius": 6 * mm});
            skSolve(sketch);
        }
        {
            var Q0;
            Q0 = qSketchRegion(id + "F16", true);
            extrude(context, id + "F17", {"entities" : qUnion([Q0]), "operationType" : NewBodyOperationType.ADD, "endBound" : BoundingType.SYMMETRIC, "depth" : 6 * mm});
        }
    });
